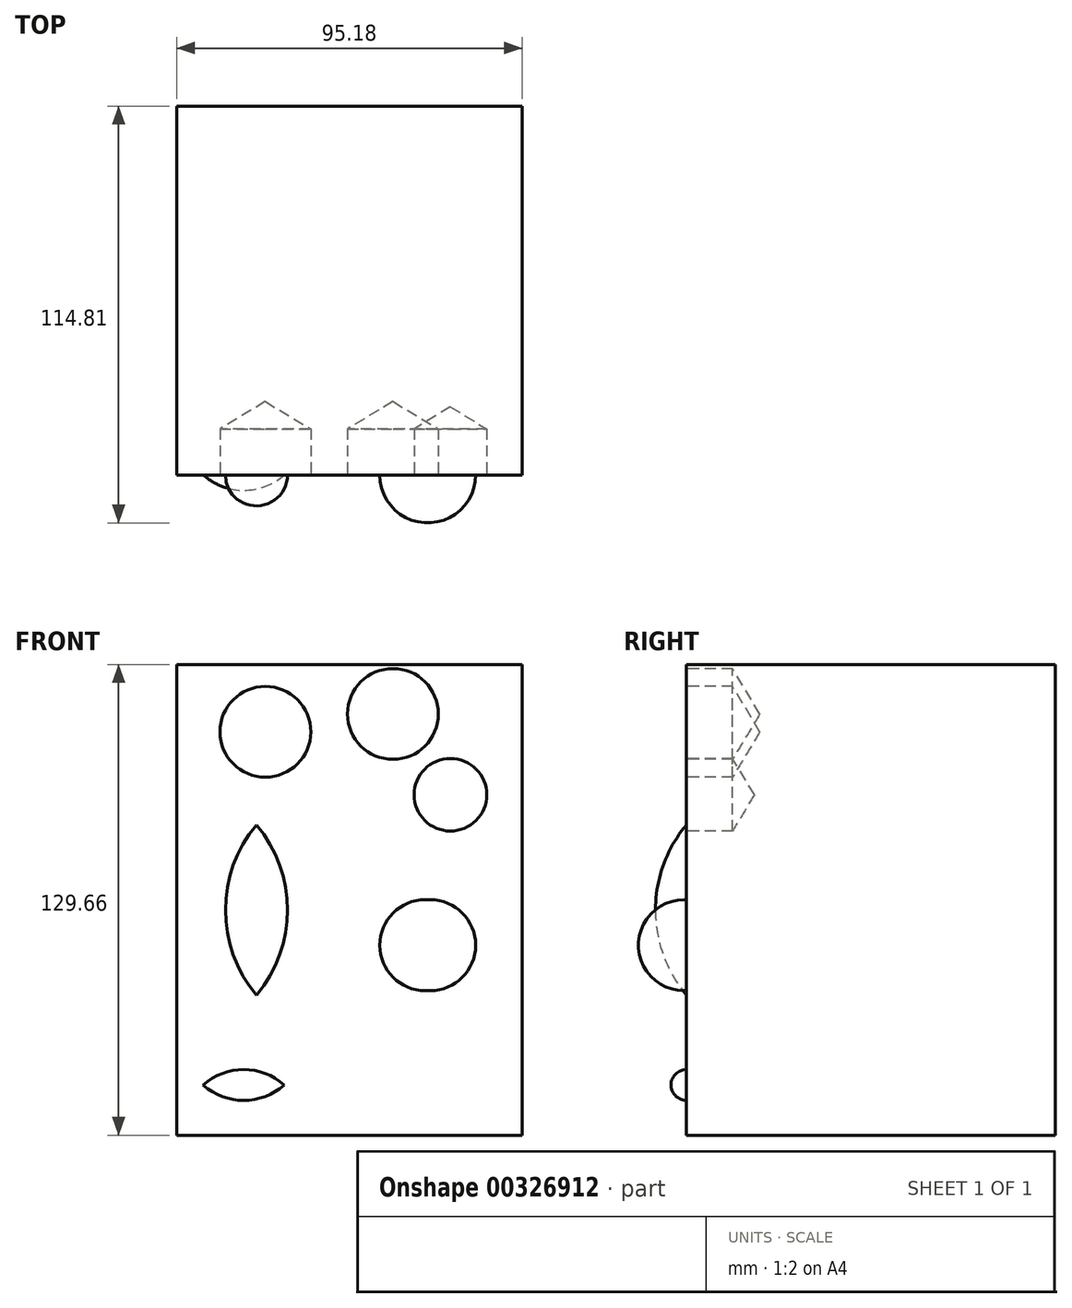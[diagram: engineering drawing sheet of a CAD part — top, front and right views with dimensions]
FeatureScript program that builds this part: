
annotation { "Feature Type Name" : "Feature", "Feature Type Description" : "" }
export const myFeature = defineFeature(function(context is Context, id is Id, definition is map)
    precondition{}
    {
        {
            var Q0;
            Q0=qCreatedBy(makeId("Front.planeOp"),FACE);
            var sketch = newSketch(context, id + "F0", { "sketchPlane" : qUnion([Q0])});
            skLineSegment(sketch, "E0.bottom", {"start": v(-47.59, -64.83) * mm, "end": v(47.59, -64.83) * mm});
            skLineSegment(sketch, "E0.top", {"start": v(-47.59, 64.83) * mm, "end": v(47.59, 64.83) * mm});
            skLineSegment(sketch, "E0.left", {"start": v(-47.59, -64.83) * mm, "end": v(-47.59, 64.83) * mm});
            skLineSegment(sketch, "E0.right", {"start": v(47.59, -64.83) * mm, "end": v(47.59, 64.83) * mm});
            skPoint(sketch, "E0.middle", {"position": v(0, 0) * mm});
            skSolve(sketch);
        }
        {
            var Q0;
            Q0 = qSketchRegion(id + "F0", true);
            extrude(context, id + "F1", {"entities" : qUnion([Q0]), "depth" : 101.6 * mm});
        }
        {
            var Q0;
            Q0=makeQuery(id+"F1.opExtrude","CAP_FACE",FACE,{"disambiguationData":[OSD([sQuery(id+"F0.wireOp",EDGE,"E0.bottom"),sQuery(id+"F0.wireOp",EDGE,"E0.top"),sQuery(id+"F0.wireOp",EDGE,"E0.left"),sQuery(id+"F0.wireOp",EDGE,"E0.right")])],"isStart":false});
            var sketch = newSketch(context, id + "F2", { "sketchPlane" : qUnion([Q0])});
            skEllipse(sketch, "E1", {"center": v(-20.8, 5.43) * mm, "majorRadius": 35.96 * mm, "minorRadius": 15.64 * mm, "majorAxis": v(0, -1)});
            skSolve(sketch);
        }
        {
            var Q0;
            Q0=makeQuery(id+"F2.imprint","IMPRINT",FACE,{"disambiguationData":[TD([[makeQuery(id+"F2.imprint","IMPRINT",EDGE,{"derivedFrom":sQuery(id+"F2.wireOp",EDGE,"E1")}),-1.0]])]});
            var sketch = newSketch(context, id + "F3", { "sketchPlane" : qUnion([Q0])});
            skPoint(sketch, "E2", {"position": v(-23.16, 46.28) * mm});
            skPoint(sketch, "E3", {"position": v(29.95, 43.1) * mm});
            skPoint(sketch, "E4", {"position": v(30.22, 112.47) * mm});
            skSolve(sketch);
        }
        {
            var Q0;
            Q0=sQuery(id+"F3.wireOp",VERTEX,"E2");
            var Q1;
            Q1=makeQuery(id+"F1.opExtrude","SWEPT_BODY",BODY,{"disambiguationData":[OSD([sQuery(id+"F0.wireOp",EDGE,"E0.bottom"),sQuery(id+"F0.wireOp",EDGE,"E0.top"),sQuery(id+"F0.wireOp",EDGE,"E0.left"),sQuery(id+"F0.wireOp",EDGE,"E0.right")])]});
            hole(context, id + "F4", {"style" : HoleStyle.SIMPLE, "endStyle" : HoleEndStyle.BLIND, "holeDiameter" : 25 * mm, "holeDepth" : 12.7 * mm, "tappedDepth" : 12.7 * mm, "tapClearance" : 3, "locations" : qUnion([Q0]), "scope" : qUnion([Q1])});
        }
        {
            var Q0;
            Q0=makeQuery(id+"F2.imprint","IMPRINT",FACE,{"disambiguationData":[TD([[makeQuery(id+"F2.imprint","IMPRINT",EDGE,{"derivedFrom":sQuery(id+"F2.wireOp",EDGE,"E1")}),-1.0]])]});
            var sketch = newSketch(context, id + "F5", { "sketchPlane" : qUnion([Q0])});
            skPoint(sketch, "E5", {"position": v(11.97, 51.2) * mm});
            skPoint(sketch, "E6", {"position": v(32.95, 39.02) * mm});
            skSolve(sketch);
        }
        {
            var Q0;
            Q0=sQuery(id+"F5.wireOp",VERTEX,"E5");
            var Q1;
            Q1=makeQuery(id+"F1.opExtrude","SWEPT_BODY",BODY,{"disambiguationData":[OSD([sQuery(id+"F0.wireOp",EDGE,"E0.bottom"),sQuery(id+"F0.wireOp",EDGE,"E0.top"),sQuery(id+"F0.wireOp",EDGE,"E0.left"),sQuery(id+"F0.wireOp",EDGE,"E0.right")])]});
            hole(context, id + "F6", {"style" : HoleStyle.SIMPLE, "endStyle" : HoleEndStyle.BLIND, "holeDiameter" : 25 * mm, "holeDepth" : 12.7 * mm, "tappedDepth" : 12.7 * mm, "tapClearance" : 3, "locations" : qUnion([Q0]), "scope" : qUnion([Q1])});
        }
        {
            var Q0;
            Q0=makeQuery(id+"F2.imprint","IMPRINT",FACE,{"disambiguationData":[TD([[makeQuery(id+"F2.imprint","IMPRINT",EDGE,{"derivedFrom":sQuery(id+"F2.wireOp",EDGE,"E1")}),-1.0]])]});
            var sketch = newSketch(context, id + "F7", { "sketchPlane" : qUnion([Q0])});
            skPoint(sketch, "E7", {"position": v(27.8, 28.94) * mm});
            skSolve(sketch);
        }
        {
            var Q0;
            Q0=sQuery(id+"F7.wireOp",VERTEX,"E7");
            var Q1;
            Q1=makeQuery(id+"F1.opExtrude","SWEPT_BODY",BODY,{"disambiguationData":[OSD([sQuery(id+"F0.wireOp",EDGE,"E0.bottom"),sQuery(id+"F0.wireOp",EDGE,"E0.top"),sQuery(id+"F0.wireOp",EDGE,"E0.left"),sQuery(id+"F0.wireOp",EDGE,"E0.right")])]});
            hole(context, id + "F8", {"style" : HoleStyle.SIMPLE, "endStyle" : HoleEndStyle.BLIND, "holeDiameter" : 20 * mm, "holeDepth" : 12.7 * mm, "tappedDepth" : 12.7 * mm, "tapClearance" : 3, "locations" : qUnion([Q0]), "scope" : qUnion([Q1])});
        }
        {
            var Q0;
            Q0=makeQuery(id+"F1.opExtrude","CAP_FACE",FACE,{"disambiguationData":[OSD([sQuery(id+"F0.wireOp",EDGE,"E0.bottom"),sQuery(id+"F0.wireOp",EDGE,"E0.top"),sQuery(id+"F0.wireOp",EDGE,"E0.left"),sQuery(id+"F0.wireOp",EDGE,"E0.right")])],"isStart":false});
            var sketch = newSketch(context, id + "F9", { "sketchPlane" : qUnion([Q0])});
            skFitSpline(sketch, "E8", {"points": [v(37, -36.37) * mm, v(34.17, -49.74) * mm, v(20.22, -53.93) * mm, v(15.66, -64.83) * mm, v(15.43, -64.83) * mm], "startDerivative": vector(1.74, -52.08) * mm, "endDerivative": vector(-5.42, 3.04) * mm});
            skFitSpline(sketch, "E9", {"points": [v(31.3, -35.26) * mm, v(25.07, -45.09) * mm, v(11.73, -49) * mm, v(7.42, -64.83) * mm], "startDerivative": vector(-13.7, -39.42) * mm, "endDerivative": vector(-2.67, -54.08) * mm});
            skSolve(sketch);
        }
        {
            var Q0;
            Q0=makeQuery(id+"F5.imprint","IMPRINT",FACE,{"disambiguationData":[TD([[makeQuery(id+"F5.imprint","IMPRINT",EDGE,{"derivedFrom":makeQuery(id+"F2.imprint","IMPRINT",EDGE,{"derivedFrom":sQuery(id+"F2.wireOp",EDGE,"E1")})}),-1.0]])]});
            var sketch = newSketch(context, id + "F10", { "sketchPlane" : qUnion([Q0])});
            skLineSegment(sketch, "E10", {"start": v(21.56, 0) * mm, "end": v(21.56, -25) * mm});
            skArc(sketch, "E11", {"start": v(21.56, 0) * mm, "mid": v(8.35, -12.5) * mm, "end": v(21.56, -25) * mm});
            skSolve(sketch);
        }
        {
            var Q0;
            Q0 = qSketchRegion(id + "F10", true);
            var Q1;
            Q1=sQuery(id+"F10.wireOp",EDGE,"E10");
            revolve(context, id + "F11", {"operationType" : NewBodyOperationType.ADD, "entities" : qUnion([Q0]), "axis" : qUnion([Q1]), "revolveType" : RevolveType.FULL});
        }
        {
            var Q0;
            Q0=makeQuery(id+"F5.imprint","IMPRINT",FACE,{"disambiguationData":[TD([[makeQuery(id+"F5.imprint","IMPRINT",EDGE,{"derivedFrom":makeQuery(id+"F2.imprint","IMPRINT",EDGE,{"derivedFrom":sQuery(id+"F2.wireOp",EDGE,"E1")})}),1.0]])]});
            var sketch = newSketch(context, id + "F12", { "sketchPlane" : qUnion([Q0])});
            skLineSegment(sketch, "E12", {"start": v(-25.6, 20.65) * mm, "end": v(-25.6, -26.26) * mm});
            skArc(sketch, "E13", {"start": v(-25.6, 20.65) * mm, "mid": v(-34.14, -2.8) * mm, "end": v(-25.6, -26.26) * mm});
            skSolve(sketch);
        }
        {
            var Q0;
            Q0 = qSketchRegion(id + "F12", true);
            var Q1;
            Q1=sQuery(id+"F12.wireOp",EDGE,"E12");
            revolve(context, id + "F13", {"operationType" : NewBodyOperationType.ADD, "entities" : qUnion([Q0]), "axis" : qUnion([Q1]), "revolveType" : RevolveType.FULL});
        }
        {
            var Q0;
            Q0=makeQuery(id+"F9.imprint","IMPRINT",FACE,{"disambiguationData":[TD([[makeQuery(id+"F9.imprint","IMPRINT",EDGE,{"derivedFrom":makeQuery(id+"F1.opExtrude","CAP_EDGE",EDGE,{"disambiguationData":[OSD([sQuery(id+"F0.wireOp",EDGE,"E0.top")])],"isStart":false})}),-1.0]])]});
            var sketch = newSketch(context, id + "F14", { "sketchPlane" : qUnion([Q0])});
            skLineSegment(sketch, "E14", {"start": v(-17.96, -51) * mm, "end": v(-40.28, -51) * mm});
            skArc(sketch, "E15", {"start": v(-17.96, -51) * mm, "mid": v(-29.12, -46.76) * mm, "end": v(-40.28, -51) * mm});
            skSolve(sketch);
        }
        {
            var Q0;
            Q0 = qSketchRegion(id + "F14", true);
            var Q1;
            Q1=sQuery(id+"F14.wireOp",EDGE,"E14");
            revolve(context, id + "F15", {"operationType" : NewBodyOperationType.ADD, "entities" : qUnion([Q0]), "axis" : qUnion([Q1]), "revolveType" : RevolveType.FULL});
        }
    });
